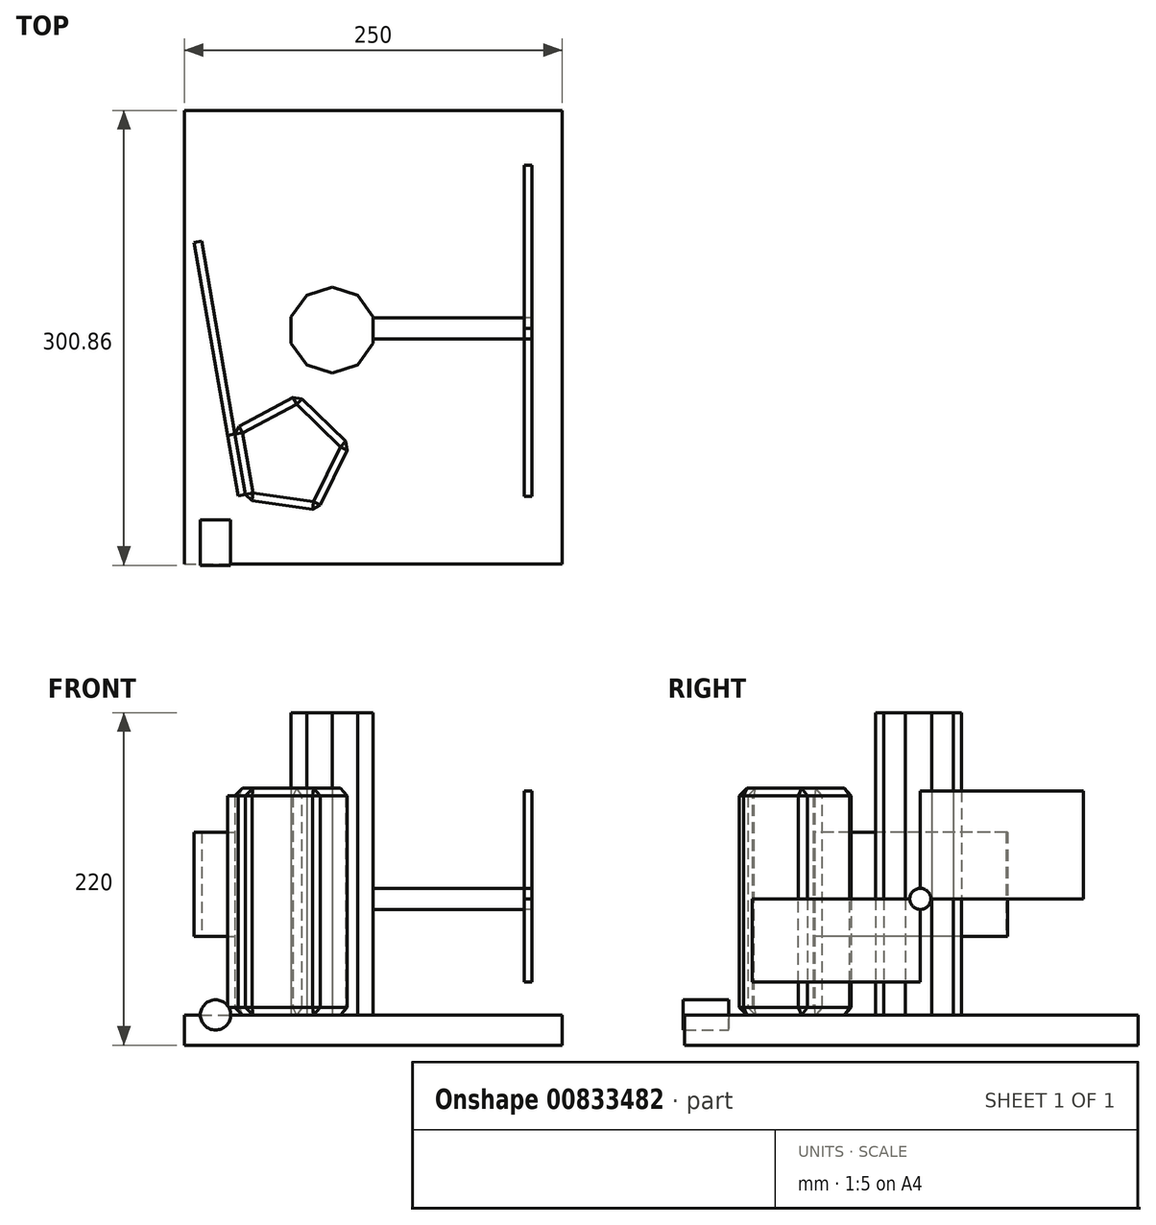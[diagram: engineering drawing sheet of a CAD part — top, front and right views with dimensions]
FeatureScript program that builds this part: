
annotation { "Feature Type Name" : "Feature", "Feature Type Description" : "" }
export const myFeature = defineFeature(function(context is Context, id is Id, definition is map)
    precondition{}
    {
        {
            var Q0;
            Q0=qCreatedBy(makeId("Front.planeOp"),FACE);
            var sketch = newSketch(context, id + "F0", { "sketchPlane" : qUnion([Q0])});
            skLineSegment(sketch, "E0.bottom", {"start": v(-99.54, 76.34) * mm, "end": v(100.46, 76.34) * mm});
            skLineSegment(sketch, "E0.top", {"start": v(-99.54, -73.66) * mm, "end": v(100.46, -73.66) * mm});
            skLineSegment(sketch, "E0.left", {"start": v(-99.54, 76.34) * mm, "end": v(-99.54, -73.66) * mm});
            skLineSegment(sketch, "E0.right", {"start": v(100.46, 76.34) * mm, "end": v(100.46, -73.66) * mm});
            skSolve(sketch);
        }
        {
            var Q0;
            Q0=qCreatedBy(makeId("Top.planeOp"),FACE);
            var sketch = newSketch(context, id + "F1", { "sketchPlane" : qUnion([Q0])});
            skLineSegment(sketch, "E1.bottom", {"start": v(-20.6, 270.86) * mm, "end": v(229.4, 270.86) * mm});
            skLineSegment(sketch, "E1.top", {"start": v(-20.6, -29.14) * mm, "end": v(229.4, -29.14) * mm});
            skLineSegment(sketch, "E1.left", {"start": v(-20.6, 270.86) * mm, "end": v(-20.6, -29.14) * mm});
            skLineSegment(sketch, "E1.right", {"start": v(229.4, 270.86) * mm, "end": v(229.4, -29.14) * mm});
            skSolve(sketch);
        }
        {
            var Q0;
            Q0=makeQuery(id+"F0.imprint","IMPRINT",FACE,{"disambiguationData":[TD([[makeQuery(id+"F0.imprint","IMPRINT",EDGE,{"derivedFrom":sQuery(id+"F0.wireOp",EDGE,"E0.bottom")}),-1.0]])]});
            var sketch = newSketch(context, id + "F2", { "sketchPlane" : qUnion([Q0])});
            skCircle(sketch, "E2", {"center": v(0, 0) * mm, "radius": 10 * mm});
            skSolve(sketch);
        }
        {
            var Q0;
            {var subQ0=sQuery(id+"F2.wireOp",EDGE,"E2");var subQ1=makeQuery(id+"F0.imprint","IMPRINT",EDGE,{"derivedFrom":sQuery(id+"F0.wireOp",EDGE,"E0.top")});var subQ2=makeQuery(id+"F2.imprint","INTERSECT",VERTEX,{"disambiguationData":[OD(0.0)],"derivedFrom":[subQ1,subQ0]});Q0=makeQuery(id+"F2.imprint","IMPRINT",FACE,{"disambiguationData":[TD([[makeQuery(id+"F2.imprint","IMPRINT",EDGE,{"disambiguationData":[TD([[subQ2,1.0]])],"derivedFrom":subQ0}),1.0]])]});}
            extrude(context, id + "F3", {"entities" : qUnion([Q0]), "depth" : 30 * mm, "offsetDistance" : 25.4 * mm});
        }
        {
            var Q0;
            Q0=makeQuery(id+"F1.imprint","IMPRINT",FACE,{"disambiguationData":[TD([[makeQuery(id+"F1.imprint","IMPRINT",EDGE,{"derivedFrom":sQuery(id+"F1.wireOp",EDGE,"E1.bottom")}),-1.0]])]});
            var sketch = newSketch(context, id + "F4", { "sketchPlane" : qUnion([Q0])});
            skCircle(sketch, "E3.cCircle", {"center": v(48.72, 42.44) * mm, "radius": 32.9 * mm, "construction": true});
            skLineSegment(sketch, "E3.0", {"start": v(88.79, 49.39) * mm, "end": v(67.7, 6.48) * mm});
            skLineSegment(sketch, "E3.1", {"start": v(67.7, 6.48) * mm, "end": v(20.4, 13.27) * mm});
            skLineSegment(sketch, "E3.2", {"start": v(20.4, 13.27) * mm, "end": v(12.22, 60.37) * mm});
            skLineSegment(sketch, "E3.3", {"start": v(12.22, 60.37) * mm, "end": v(54.5, 82.7) * mm});
            skLineSegment(sketch, "E3.4", {"start": v(54.5, 82.7) * mm, "end": v(88.79, 49.39) * mm});
            skPoint(sketch, "E3.0.midPoint", {"position": v(78.25, 27.94) * mm});
            skSolve(sketch);
        }
        {
            var Q0;
            Q0=makeQuery(id+"F4.imprint","IMPRINT",FACE,{"disambiguationData":[TD([[makeQuery(id+"F4.imprint","IMPRINT",EDGE,{"derivedFrom":sQuery(id+"F4.wireOp",EDGE,"E3.0")}),-1.0]])]});
            extrude(context, id + "F5", {"entities" : qUnion([Q0]), "depth" : 150 * mm, "offsetDistance" : 25.4 * mm});
        }
        {
            var Q0;
            Q0=makeQuery(id+"F5.opExtrude","SWEPT_EDGE",EDGE,{"disambiguationData":[OSD([sQuery(id+"F4.wireOp",EDGE,"E3.1"),sQuery(id+"F4.wireOp",EDGE,"E3.2")])]});
            var Q1;
            Q1=makeQuery(id+"F5.opExtrude","SWEPT_EDGE",EDGE,{"disambiguationData":[OSD([sQuery(id+"F4.wireOp",EDGE,"E3.0"),sQuery(id+"F4.wireOp",EDGE,"E3.1")])]});
            var Q2;
            Q2=makeQuery(id+"F5.opExtrude","SWEPT_EDGE",EDGE,{"disambiguationData":[OSD([sQuery(id+"F4.wireOp",EDGE,"E3.0"),sQuery(id+"F4.wireOp",EDGE,"E3.4")])]});
            var Q3;
            Q3=makeQuery(id+"F5.opExtrude","CAP_EDGE",EDGE,{"disambiguationData":[OSD([sQuery(id+"F4.wireOp",EDGE,"E3.2")])],"isStart":false});
            var Q4;
            Q4=makeQuery(id+"F5.opExtrude","CAP_EDGE",EDGE,{"disambiguationData":[OSD([sQuery(id+"F4.wireOp",EDGE,"E3.1")])],"isStart":false});
            var Q5;
            Q5=makeQuery(id+"F5.opExtrude","CAP_EDGE",EDGE,{"disambiguationData":[OSD([sQuery(id+"F4.wireOp",EDGE,"E3.3")])],"isStart":false});
            var Q6;
            Q6=makeQuery(id+"F5.opExtrude","CAP_EDGE",EDGE,{"disambiguationData":[OSD([sQuery(id+"F4.wireOp",EDGE,"E3.4")])],"isStart":false});
            var Q7;
            Q7=makeQuery(id+"F5.opExtrude","CAP_EDGE",EDGE,{"disambiguationData":[OSD([sQuery(id+"F4.wireOp",EDGE,"E3.0")])],"isStart":false});
            var Q8;
            Q8=makeQuery(id+"F5.opExtrude","SWEPT_EDGE",EDGE,{"disambiguationData":[OSD([sQuery(id+"F4.wireOp",EDGE,"E3.3"),sQuery(id+"F4.wireOp",EDGE,"E3.4")])]});
            var Q9;
            Q9=makeQuery(id+"F5.opExtrude","SWEPT_EDGE",EDGE,{"disambiguationData":[OSD([sQuery(id+"F4.wireOp",EDGE,"E3.2"),sQuery(id+"F4.wireOp",EDGE,"E3.3")])]});
            var Q10;
            Q10=makeQuery(id+"F5.opExtrude","CAP_EDGE",EDGE,{"disambiguationData":[OSD([sQuery(id+"F4.wireOp",EDGE,"E3.3")])],"isStart":true});
            var Q11;
            Q11=makeQuery(id+"F5.opExtrude","CAP_EDGE",EDGE,{"disambiguationData":[OSD([sQuery(id+"F4.wireOp",EDGE,"E3.4")])],"isStart":true});
            var Q12;
            Q12=makeQuery(id+"F5.opExtrude","CAP_EDGE",EDGE,{"disambiguationData":[OSD([sQuery(id+"F4.wireOp",EDGE,"E3.2")])],"isStart":true});
            var Q13;
            Q13=makeQuery(id+"F5.opExtrude","CAP_EDGE",EDGE,{"disambiguationData":[OSD([sQuery(id+"F4.wireOp",EDGE,"E3.1")])],"isStart":true});
            var Q14;
            Q14=makeQuery(id+"F5.opExtrude","CAP_EDGE",EDGE,{"disambiguationData":[OSD([sQuery(id+"F4.wireOp",EDGE,"E3.0")])],"isStart":true});
            chamfer(context, id + "F6", {"entities" : qUnion([Q0, Q1, Q2, Q3, Q4, Q5, Q6, Q7, Q8, Q9, Q10, Q11, Q12, Q13, Q14]), "width" : 5.08 * mm, "tangentPropagation" : true});
        }
        {
            var Q0;
            Q0=makeQuery(id+"F5.opExtrude","SWEPT_FACE",FACE,{"disambiguationData":[OSD([sQuery(id+"F4.wireOp",EDGE,"E3.2")])]});
            var sketch = newSketch(context, id + "F7", { "sketchPlane" : qUnion([Q0])});
            skLineSegment(sketch, "E4.bottom", {"start": v(-183.34, 120.92) * mm, "end": v(16.28, 120.92) * mm});
            skLineSegment(sketch, "E4.top", {"start": v(-183.34, 51.85) * mm, "end": v(16.28, 51.85) * mm});
            skLineSegment(sketch, "E4.left", {"start": v(-183.34, 120.92) * mm, "end": v(-183.34, 51.85) * mm});
            skLineSegment(sketch, "E4.right", {"start": v(16.28, 120.92) * mm, "end": v(16.28, 51.85) * mm});
            skSolve(sketch);
        }
        {
            var Q0;
            {var subQ0=sQuery(id+"F7.wireOp",EDGE,"E4.left");Q0=makeQuery(id+"F7.imprint","IMPRINT",FACE,{"disambiguationData":[TD([[makeQuery(id+"F7.imprint","IMPRINT",EDGE,{"derivedFrom":subQ0}),1.0]])]});}
            extrude(context, id + "F8", {"entities" : qUnion([Q0]), "depth" : 5 * mm, "offsetDistance" : 25.4 * mm});
        }
        {
            var Q0;
            Q0=makeQuery(id+"F5.opExtrude","SWEPT_FACE",FACE,{"disambiguationData":[OSD([sQuery(id+"F4.wireOp",EDGE,"E3.2")])]});
            extrude(context, id + "F9", {"entities" : qUnion([Q0]), "depth" : 5 * mm, "offsetDistance" : 25.4 * mm});
        }
        {
            var Q0;
            Q0=makeQuery(id+"F1.imprint","IMPRINT",FACE,{"disambiguationData":[TD([[makeQuery(id+"F1.imprint","IMPRINT",EDGE,{"derivedFrom":sQuery(id+"F1.wireOp",EDGE,"E1.bottom")}),-1.0]])]});
            extrude(context, id + "F10", {"entities" : qUnion([Q0]), "oppositeDirection" : true, "depth" : 20 * mm, "offsetDistance" : 25.4 * mm});
        }
        {
            var Q0;
            Q0=makeQuery(id+"F10.opExtrude","CAP_FACE",FACE,{"disambiguationData":[OSD([sQuery(id+"F1.wireOp",EDGE,"E1.bottom"),sQuery(id+"F1.wireOp",EDGE,"E1.top"),sQuery(id+"F1.wireOp",EDGE,"E1.left"),sQuery(id+"F1.wireOp",EDGE,"E1.right")])],"isStart":true});
            var sketch = newSketch(context, id + "F11", { "sketchPlane" : qUnion([Q0])});
            skCircle(sketch, "E5.cCircle", {"center": v(77.13, 125.68) * mm, "radius": 27.1 * mm, "construction": true});
            skLineSegment(sketch, "E5.0", {"start": v(104.24, 134.48) * mm, "end": v(104.24, 116.87) * mm});
            skLineSegment(sketch, "E5.1", {"start": v(104.24, 116.87) * mm, "end": v(93.88, 102.62) * mm});
            skLineSegment(sketch, "E5.2", {"start": v(93.88, 102.62) * mm, "end": v(77.13, 97.17) * mm});
            skLineSegment(sketch, "E5.3", {"start": v(77.13, 97.17) * mm, "end": v(60.37, 102.62) * mm});
            skLineSegment(sketch, "E5.4", {"start": v(60.37, 102.62) * mm, "end": v(50.02, 116.87) * mm});
            skLineSegment(sketch, "E5.5", {"start": v(50.02, 116.87) * mm, "end": v(50.02, 134.48) * mm});
            skLineSegment(sketch, "E5.6", {"start": v(50.02, 134.48) * mm, "end": v(60.37, 148.74) * mm});
            skLineSegment(sketch, "E5.7", {"start": v(60.37, 148.74) * mm, "end": v(77.13, 154.18) * mm});
            skLineSegment(sketch, "E5.8", {"start": v(77.13, 154.18) * mm, "end": v(93.88, 148.74) * mm});
            skLineSegment(sketch, "E5.9", {"start": v(93.88, 148.74) * mm, "end": v(104.24, 134.48) * mm});
            skPoint(sketch, "E5.0.midPoint", {"position": v(104.24, 125.68) * mm});
            skSolve(sketch);
        }
        {
            var Q0;
            Q0=makeQuery(id+"F11.imprint","IMPRINT",FACE,{"disambiguationData":[TD([[makeQuery(id+"F11.imprint","IMPRINT",EDGE,{"derivedFrom":sQuery(id+"F11.wireOp",EDGE,"E5.0")}),-1.0]])]});
            extrude(context, id + "F12", {"entities" : qUnion([Q0]), "operationType" : NewBodyOperationType.ADD, "depth" : 200 * mm, "offsetDistance" : 25.4 * mm});
        }
        {
            var Q0;
            Q0=makeQuery(id+"F12.opExtrude","SWEPT_FACE",FACE,{"disambiguationData":[OSD([sQuery(id+"F11.wireOp",EDGE,"E5.0")])]});
            var sketch = newSketch(context, id + "F13", { "sketchPlane" : qUnion([Q0])});
            skCircle(sketch, "E6", {"center": v(126.79, 76.78) * mm, "radius": 6.98 * mm});
            skSolve(sketch);
        }
        {
            var Q0;
            Q0=makeQuery(id+"F13.imprint","IMPRINT",FACE,{"disambiguationData":[TD([[makeQuery(id+"F13.imprint","IMPRINT",EDGE,{"derivedFrom":sQuery(id+"F13.wireOp",EDGE,"E6")}),1.0]])]});
            extrude(context, id + "F14", {"entities" : qUnion([Q0]), "operationType" : NewBodyOperationType.ADD, "depth" : 100 * mm, "offsetDistance" : 25.4 * mm});
        }
        {
            var Q0;
            Q0=makeQuery(id+"F14.opExtrude","CAP_FACE",FACE,{"disambiguationData":[OSD([sQuery(id+"F13.wireOp",EDGE,"E6")])],"isStart":false});
            var sketch = newSketch(context, id + "F15", { "sketchPlane" : qUnion([Q0])});
            skLineSegment(sketch, "E7.bottom", {"start": v(126.79, 76.78) * mm, "end": v(234.63, 76.78) * mm});
            skLineSegment(sketch, "E7.top", {"start": v(126.79, 148.3) * mm, "end": v(234.63, 148.3) * mm});
            skLineSegment(sketch, "E7.left", {"start": v(126.79, 76.78) * mm, "end": v(126.79, 148.3) * mm});
            skLineSegment(sketch, "E7.right", {"start": v(234.63, 76.78) * mm, "end": v(234.63, 148.3) * mm});
            skLineSegment(sketch, "E8.bottom", {"start": v(126.79, 76.78) * mm, "end": v(15.6, 76.78) * mm});
            skLineSegment(sketch, "E8.top", {"start": v(126.79, 21.73) * mm, "end": v(15.6, 21.73) * mm});
            skLineSegment(sketch, "E8.left", {"start": v(126.79, 76.78) * mm, "end": v(126.79, 21.73) * mm});
            skLineSegment(sketch, "E8.right", {"start": v(15.6, 76.78) * mm, "end": v(15.6, 21.73) * mm});
            skSolve(sketch);
        }
        {
            var Q0;
            {var subQ2=sQuery(id+"F15.wireOp",EDGE,"E7.top");Q0=makeQuery(id+"F15.imprint","IMPRINT",FACE,{"disambiguationData":[TD([[makeQuery(id+"F15.imprint","IMPRINT",EDGE,{"derivedFrom":subQ2}),-1.0]])]});}
            var Q1;
            {var subQ2=sQuery(id+"F15.wireOp",EDGE,"E8.top");Q1=makeQuery(id+"F15.imprint","IMPRINT",FACE,{"disambiguationData":[TD([[makeQuery(id+"F15.imprint","IMPRINT",EDGE,{"derivedFrom":subQ2}),-1.0]])]});}
            extrude(context, id + "F16", {"entities" : qUnion([Q0, Q1]), "depth" : 5 * mm, "offsetDistance" : 25.4 * mm});
        }
    });
